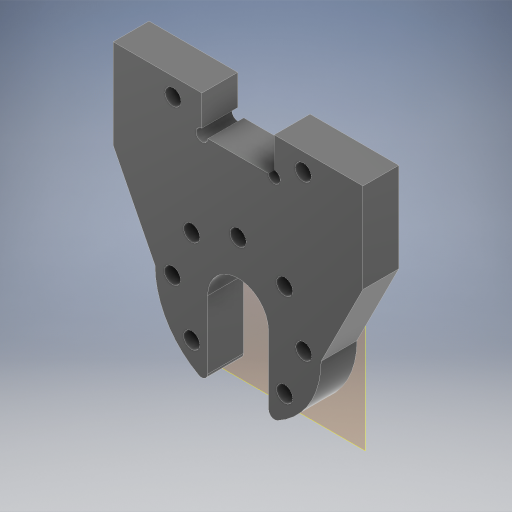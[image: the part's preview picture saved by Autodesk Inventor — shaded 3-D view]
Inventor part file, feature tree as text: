
AUTODESK INVENTOR PART (.ipt)
format: ipt  version: 2024 (Build 280153000, 153)  size: 327,168 bytes
history: native  units: in
note: dims shown in document units (in); Inventor stores cm internally (conversion verified against a paired STEP export)
features: other x3, extrude x2, sketch x2, fillet x1, reference x1
ambient origin geometry x8: Origin, YZ Plane, XZ Plane, XY Plane, X Axis, Y Axis, Z Axis, Center Point
bodies: Body1 (feature_tree)
feature tree (9):
  other  "작업 평면1"
  extrude  "돌출7"  Depth=0.0039in
  fillet  "모깎기3"  Radius=0.1063in
  extrude  "돌출8"  Depth=3.1496in TaperAngle=360.0deg
  sketch  "스케치1"
  reference  "참조1"
  sketch  "스케치2"
  other  "조립품12"
  other  "64-106Horn:1"
